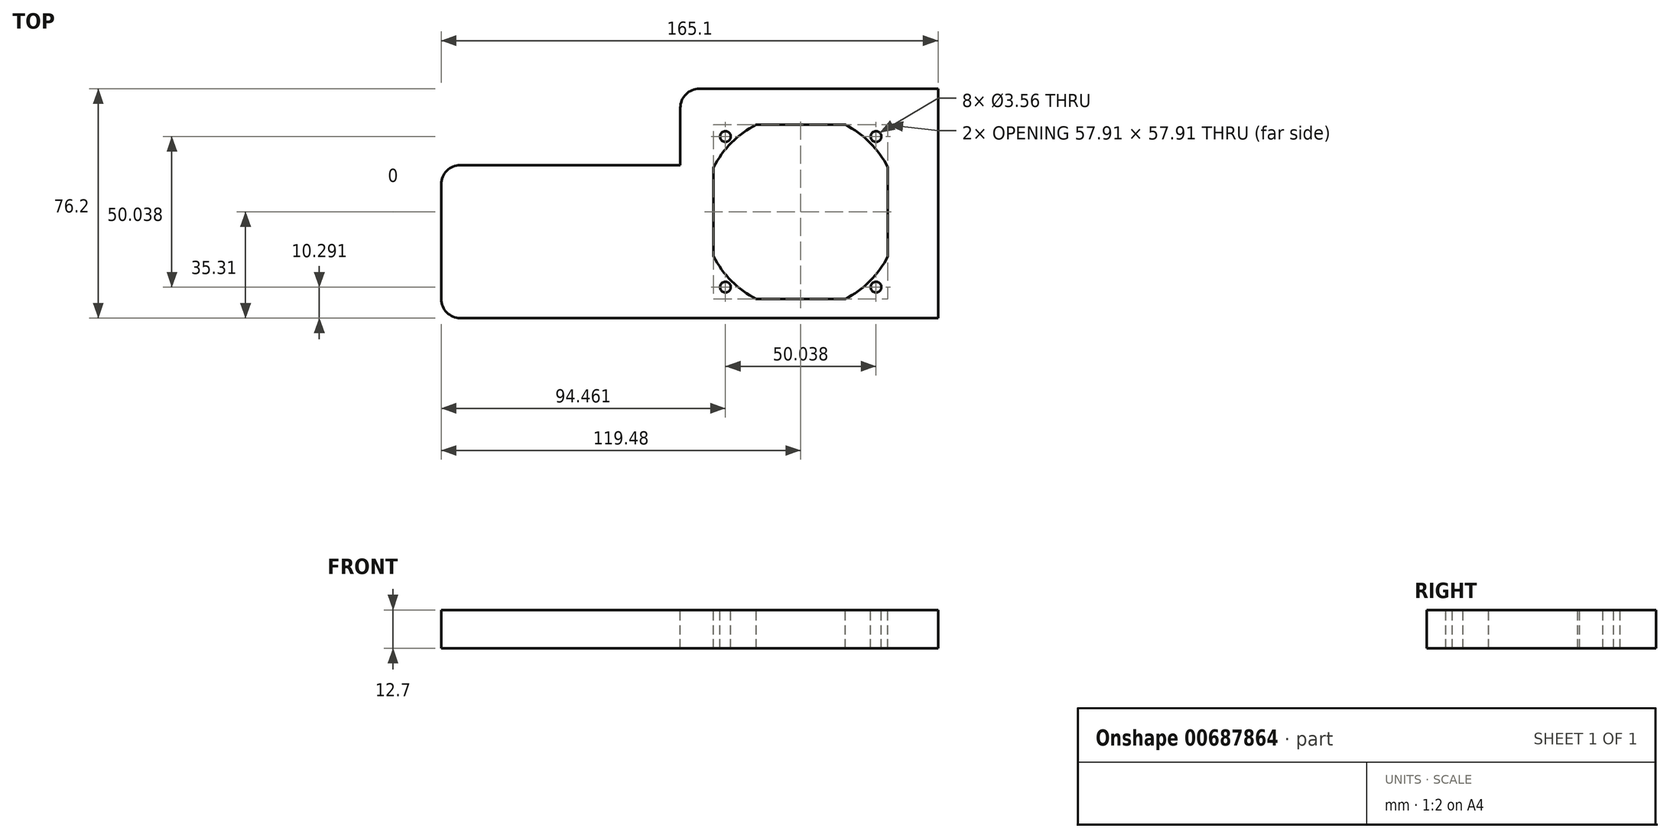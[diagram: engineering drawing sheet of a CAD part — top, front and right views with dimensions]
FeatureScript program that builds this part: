
annotation { "Feature Type Name" : "Feature", "Feature Type Description" : "" }
export const myFeature = defineFeature(function(context is Context, id is Id, definition is map)
    precondition{}
    {
        {
            var Q0;
            Q0=qCreatedBy(makeId("Top.planeOp"),FACE);
            var sketch = newSketch(context, id + "F0", { "sketchPlane" : qUnion([Q0])});
            skArc(sketch, "E0", {"start": v(-14.78, 28.96) * mm, "mid": v(-22.99, 22.99) * mm, "end": v(-28.96, 14.78) * mm});
            skLineSegment(sketch, "E1.bottom", {"start": v(14.78, -28.96) * mm, "end": v(-14.78, -28.96) * mm});
            skLineSegment(sketch, "E1.top", {"start": v(14.78, 28.96) * mm, "end": v(-14.78, 28.96) * mm});
            skLineSegment(sketch, "E1.left", {"start": v(28.96, -14.78) * mm, "end": v(28.96, 14.78) * mm});
            skLineSegment(sketch, "E1.right", {"start": v(-28.96, -14.78) * mm, "end": v(-28.96, 14.78) * mm});
            skPoint(sketch, "E2", {"position": v(-14.78, 28.96) * mm});
            skPoint(sketch, "E3", {"position": v(-28.96, 14.78) * mm});
            skPoint(sketch, "E4", {"position": v(14.78, 28.96) * mm});
            skPoint(sketch, "E5", {"position": v(28.96, 14.78) * mm});
            skPoint(sketch, "E6", {"position": v(28.96, -14.78) * mm});
            skPoint(sketch, "E7", {"position": v(14.78, -28.96) * mm});
            skPoint(sketch, "E8", {"position": v(-14.78, -28.96) * mm});
            skPoint(sketch, "E9", {"position": v(-28.96, -14.78) * mm});
            skPoint(sketch, "E10.orphan", {"position": v(28.96, 28.96) * mm});
            skArc(sketch, "E11.trimOffspring", {"start": v(28.96, 14.78) * mm, "mid": v(22.99, 22.99) * mm, "end": v(14.78, 28.96) * mm});
            skPoint(sketch, "E12.orphan", {"position": v(-28.96, 28.96) * mm});
            skArc(sketch, "E13.trimOffspring", {"start": v(-28.96, -14.78) * mm, "mid": v(-22.99, -22.99) * mm, "end": v(-14.78, -28.96) * mm});
            skPoint(sketch, "E14.orphan", {"position": v(-28.96, -28.96) * mm});
            skArc(sketch, "E15.trimOffspring", {"start": v(14.78, -28.96) * mm, "mid": v(22.99, -22.99) * mm, "end": v(28.96, -14.78) * mm});
            skPoint(sketch, "E16.orphan", {"position": v(28.96, -28.96) * mm});
            skLineSegment(sketch, "E17.bottom", {"start": v(25.02, -25.02) * mm, "end": v(-25.02, -25.02) * mm, "construction": true});
            skLineSegment(sketch, "E17.top", {"start": v(25.02, 25.02) * mm, "end": v(-25.02, 25.02) * mm, "construction": true});
            skLineSegment(sketch, "E17.left", {"start": v(25.02, -25.02) * mm, "end": v(25.02, 25.02) * mm, "construction": true});
            skLineSegment(sketch, "E17.right", {"start": v(-25.02, -25.02) * mm, "end": v(-25.02, 25.02) * mm, "construction": true});
            skLineSegment(sketch, "E18", {"start": v(28.96, 0) * mm, "end": v(40.07, 0) * mm, "construction": true});
            skLineSegment(sketch, "E19", {"start": v(0, -28.96) * mm, "end": v(0, -35.3) * mm, "construction": true});
            skLineSegment(sketch, "E20", {"start": v(0, -35.3) * mm, "end": v(32.92, -35.3) * mm, "construction": true});
            skLineSegment(sketch, "E21.bottom", {"start": v(32.92, -35.3) * mm, "end": v(-113.13, -35.3) * mm});
            skLineSegment(sketch, "E21.top", {"start": v(32.92, 40.9) * mm, "end": v(-33.66, 40.9) * mm});
            skLineSegment(sketch, "E21.right", {"start": v(-119.48, -28.96) * mm, "end": v(-119.48, 9.14) * mm});
            skLineSegment(sketch, "E22", {"start": v(-40, 34.54) * mm, "end": v(-40, 15.5) * mm});
            skLineSegment(sketch, "E23", {"start": v(-40, 15.5) * mm, "end": v(-113.13, 15.5) * mm});
            skPoint(sketch, "E24.visualSharp", {"position": v(-40, 40.9) * mm});
            skArc(sketch, "E24.filletArc", {"start": v(-33.66, 40.9) * mm, "mid": v(-38.15, 39.03) * mm, "end": v(-40, 34.54) * mm});
            skPoint(sketch, "E25.visualSharp", {"position": v(39.27, 40.9) * mm});
            skPoint(sketch, "E26.visualSharp", {"position": v(39.27, -35.3) * mm});
            skPoint(sketch, "E27.visualSharp", {"position": v(-119.48, -35.3) * mm});
            skArc(sketch, "E27.filletArc", {"start": v(-119.48, -28.96) * mm, "mid": v(-117.62, -33.45) * mm, "end": v(-113.13, -35.3) * mm});
            skPoint(sketch, "E28.visualSharp", {"position": v(-119.48, 15.5) * mm});
            skArc(sketch, "E28.filletArc", {"start": v(-113.13, 15.5) * mm, "mid": v(-117.62, 13.63) * mm, "end": v(-119.48, 9.14) * mm});
            skCircle(sketch, "E29", {"center": v(-25.02, 25.02) * mm, "radius": 1.78 * mm});
            skCircle(sketch, "E30", {"center": v(25.02, 25.02) * mm, "radius": 1.78 * mm});
            skCircle(sketch, "E31", {"center": v(25.02, -25.02) * mm, "radius": 1.78 * mm});
            skCircle(sketch, "E32", {"center": v(-25.02, -25.02) * mm, "radius": 1.78 * mm});
            skPoint(sketch, "E33.middle", {"position": v(34.51, 0) * mm});
            skLineSegment(sketch, "E34", {"start": v(39.27, 40.9) * mm, "end": v(45.62, 40.9) * mm, "construction": true});
            skLineSegment(sketch, "E35", {"start": v(32.92, 40.9) * mm, "end": v(45.62, 40.9) * mm});
            skLineSegment(sketch, "E36", {"start": v(45.62, 40.9) * mm, "end": v(45.62, -35.3) * mm});
            skLineSegment(sketch, "E37", {"start": v(45.62, -35.3) * mm, "end": v(32.92, -35.3) * mm});
            skSolve(sketch);
        }
        {
            var Q0;
            Q0=makeQuery(id+"F0.imprint","IMPRINT",FACE,{"disambiguationData":[TD([[makeQuery(id+"F0.imprint","IMPRINT",EDGE,{"derivedFrom":sQuery(id+"F0.wireOp",EDGE,"E0")}),-1.0]])]});
            extrude(context, id + "F1", {"entities" : qUnion([Q0]), "depth" : -2 / 406.4 * mm, "offsetDistance" : 25.4 * mm});
        }
        {
            var Q0;
            Q0=makeQuery(id+"F0.imprint","IMPRINT",FACE,{"disambiguationData":[TD([[makeQuery(id+"F0.imprint","IMPRINT",EDGE,{"derivedFrom":sQuery(id+"F0.wireOp",EDGE,"cztJWDYq-EYQ1-ocjy-S0AX-zjgeVbo6ku81.bottom")}),1.0]])]});
            var Q1;
            Q1=makeQuery(id+"F1.opExtrude","CAP_FACE",FACE,{"disambiguationData":[OSD([sQuery(id+"F0.wireOp",EDGE,"E0"),sQuery(id+"F0.wireOp",EDGE,"E1.bottom"),sQuery(id+"F0.wireOp",EDGE,"E1.top"),sQuery(id+"F0.wireOp",EDGE,"E1.left"),sQuery(id+"F0.wireOp",EDGE,"E1.right"),sQuery(id+"F0.wireOp",EDGE,"E11.trimOffspring"),sQuery(id+"F0.wireOp",EDGE,"E13.trimOffspring"),sQuery(id+"F0.wireOp",EDGE,"E15.trimOffspring"),sQuery(id+"F0.wireOp",EDGE,"E21.bottom"),sQuery(id+"F0.wireOp",EDGE,"E21.top"),sQuery(id+"F0.wireOp",EDGE,"E21.right"),sQuery(id+"F0.wireOp",EDGE,"E22"),sQuery(id+"F0.wireOp",EDGE,"E23"),sQuery(id+"F0.wireOp",EDGE,"E24.filletArc"),sQuery(id+"F0.wireOp",EDGE,"E27.filletArc"),sQuery(id+"F0.wireOp",EDGE,"E28.filletArc"),sQuery(id+"F0.wireOp",EDGE,"E29"),sQuery(id+"F0.wireOp",EDGE,"E30"),sQuery(id+"F0.wireOp",EDGE,"E31"),sQuery(id+"F0.wireOp",EDGE,"E32"),sQuery(id+"F0.wireOp",EDGE,"E35"),sQuery(id+"F0.wireOp",EDGE,"E36"),sQuery(id+"F0.wireOp",EDGE,"E37")])],"isStart":false});
            extrude(context, id + "F2", {"entities" : qUnion([Q0, Q1]), "depth" : 12.7 * mm, "offsetDistance" : 25.4 * mm});
        }
    });
